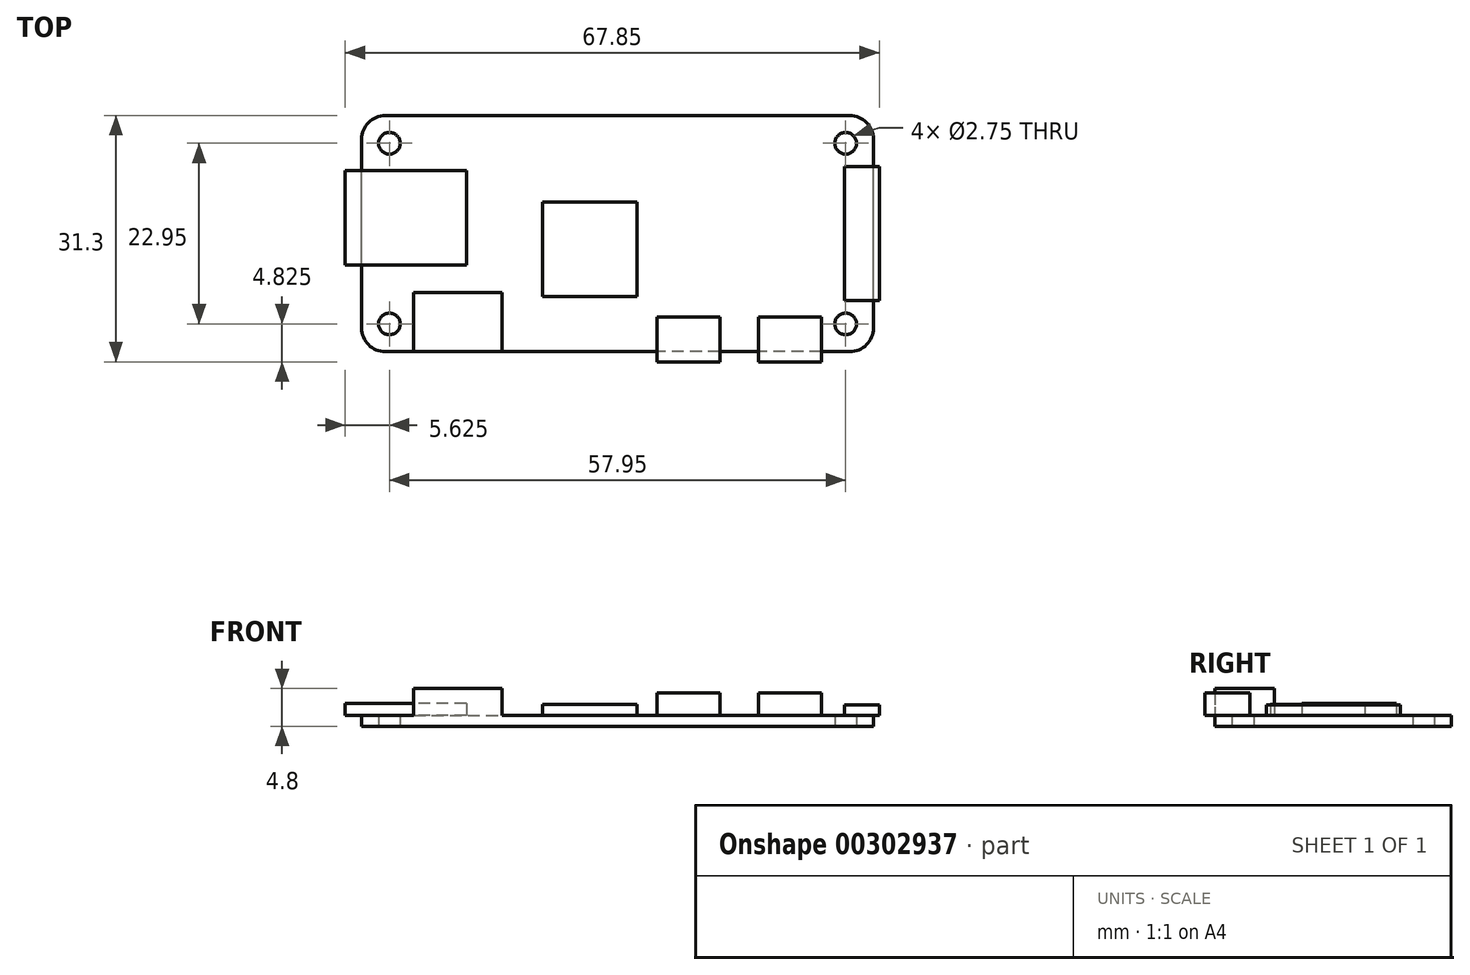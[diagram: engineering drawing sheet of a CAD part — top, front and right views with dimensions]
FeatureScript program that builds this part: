
annotation { "Feature Type Name" : "Feature", "Feature Type Description" : "" }
export const myFeature = defineFeature(function(context is Context, id is Id, definition is map)
    precondition{}
    {
        {
            var Q0;
            Q0=qCreatedBy(makeId("Top.planeOp"),FACE);
            var sketch = newSketch(context, id + "F0", { "sketchPlane" : qUnion([Q0])});
            skLineSegment(sketch, "E0.bottom", {"start": v(29.5, -15) * mm, "end": v(-29.5, -15) * mm});
            skLineSegment(sketch, "E0.top", {"start": v(29.5, 15) * mm, "end": v(-29.5, 15) * mm});
            skLineSegment(sketch, "E0.left", {"start": v(32.5, -12) * mm, "end": v(32.5, 12) * mm});
            skLineSegment(sketch, "E0.right", {"start": v(-32.5, -12) * mm, "end": v(-32.5, 12) * mm});
            skPoint(sketch, "E0.middle", {"position": v(0, 0) * mm});
            skCircle(sketch, "E1", {"center": v(-28.98, 11.47) * mm, "radius": 1.38 * mm});
            skCircle(sketch, "E2", {"center": v(28.98, 11.47) * mm, "radius": 1.38 * mm});
            skCircle(sketch, "E3", {"center": v(-28.98, -11.47) * mm, "radius": 1.38 * mm});
            skCircle(sketch, "E4", {"center": v(28.98, -11.47) * mm, "radius": 1.38 * mm});
            skPoint(sketch, "E5.visualSharp", {"position": v(-32.5, 15) * mm});
            skArc(sketch, "E5.filletArc", {"start": v(-29.5, 15) * mm, "mid": v(-31.62, 14.12) * mm, "end": v(-32.5, 12) * mm});
            skPoint(sketch, "E6.visualSharp", {"position": v(32.5, 15) * mm});
            skArc(sketch, "E6.filletArc", {"start": v(32.5, 12) * mm, "mid": v(31.62, 14.12) * mm, "end": v(29.5, 15) * mm});
            skPoint(sketch, "E7.visualSharp", {"position": v(32.5, -15) * mm});
            skArc(sketch, "E7.filletArc", {"start": v(29.5, -15) * mm, "mid": v(31.62, -14.12) * mm, "end": v(32.5, -12) * mm});
            skPoint(sketch, "E8.visualSharp", {"position": v(-32.5, -15) * mm});
            skArc(sketch, "E8.filletArc", {"start": v(-32.5, -12) * mm, "mid": v(-31.62, -14.12) * mm, "end": v(-29.5, -15) * mm});
            skSolve(sketch);
        }
        {
            var Q0;
            Q0=qSketchRegion(id+"F0",true);
            extrude(context, id + "F1", {"entities" : qUnion([Q0]), "depth" : 1.4 * mm});
        }
        {
            var Q0;
            Q0=makeQuery(id+"F1.opExtrude","CAP_FACE",FACE,{"disambiguationData":[OSD([sQuery(id+"F0.wireOp",EDGE,"E0.bottom"),sQuery(id+"F0.wireOp",EDGE,"E0.top"),sQuery(id+"F0.wireOp",EDGE,"E0.left"),sQuery(id+"F0.wireOp",EDGE,"E0.right"),sQuery(id+"F0.wireOp",EDGE,"E1"),sQuery(id+"F0.wireOp",EDGE,"E2"),sQuery(id+"F0.wireOp",EDGE,"E3"),sQuery(id+"F0.wireOp",EDGE,"E4"),sQuery(id+"F0.wireOp",EDGE,"E5.filletArc"),sQuery(id+"F0.wireOp",EDGE,"E6.filletArc"),sQuery(id+"F0.wireOp",EDGE,"E7.filletArc"),sQuery(id+"F0.wireOp",EDGE,"E8.filletArc")])],"isStart":false});
            var sketch = newSketch(context, id + "F2", { "sketchPlane" : qUnion([Q0])});
            skLineSegment(sketch, "E9.bottom", {"start": v(2.5, -8) * mm, "end": v(-9.5, -8) * mm});
            skLineSegment(sketch, "E9.top", {"start": v(2.5, 4) * mm, "end": v(-9.5, 4) * mm});
            skLineSegment(sketch, "E9.left", {"start": v(2.5, -8) * mm, "end": v(2.5, 4) * mm});
            skLineSegment(sketch, "E9.right", {"start": v(-9.5, -8) * mm, "end": v(-9.5, 4) * mm});
            skPoint(sketch, "E9.middle", {"position": v(-3.5, -2) * mm});
            skLineSegment(sketch, "E10.bottom", {"start": v(33.25, -8.5) * mm, "end": v(28.85, -8.5) * mm});
            skLineSegment(sketch, "E10.top", {"start": v(33.25, 8.5) * mm, "end": v(28.85, 8.5) * mm});
            skLineSegment(sketch, "E10.left", {"start": v(33.25, -8.5) * mm, "end": v(33.25, 8.5) * mm});
            skLineSegment(sketch, "E10.right", {"start": v(28.85, -8.5) * mm, "end": v(28.85, 8.5) * mm});
            skPoint(sketch, "E10.middle", {"position": v(31.05, 0) * mm});
            skPoint(sketch, "E11", {"position": v(32.5, 0) * mm});
            skLineSegment(sketch, "E12.bottom", {"start": v(-19.2, -4) * mm, "end": v(-34.6, -4) * mm});
            skLineSegment(sketch, "E12.top", {"start": v(-19.2, 8) * mm, "end": v(-34.6, 8) * mm});
            skLineSegment(sketch, "E12.left", {"start": v(-19.2, -4) * mm, "end": v(-19.2, 8) * mm});
            skLineSegment(sketch, "E12.right", {"start": v(-34.6, -4) * mm, "end": v(-34.6, 8) * mm});
            skPoint(sketch, "E12.middle", {"position": v(-26.9, 2) * mm});
            skLineSegment(sketch, "E13.bottom", {"start": v(-25.9, -15) * mm, "end": v(-14.7, -15) * mm});
            skLineSegment(sketch, "E13.top", {"start": v(-25.9, -7.5) * mm, "end": v(-14.7, -7.5) * mm});
            skLineSegment(sketch, "E13.left", {"start": v(-25.9, -15) * mm, "end": v(-25.9, -7.5) * mm});
            skLineSegment(sketch, "E13.right", {"start": v(-14.7, -15) * mm, "end": v(-14.7, -7.5) * mm});
            skLineSegment(sketch, "E14.bottom", {"start": v(5, -16.3) * mm, "end": v(13, -16.3) * mm});
            skLineSegment(sketch, "E14.top", {"start": v(5, -10.6) * mm, "end": v(13, -10.6) * mm});
            skLineSegment(sketch, "E14.left", {"start": v(5, -16.3) * mm, "end": v(5, -10.6) * mm});
            skLineSegment(sketch, "E14.right", {"start": v(13, -16.3) * mm, "end": v(13, -10.6) * mm});
            skLineSegment(sketch, "E15.bottom", {"start": v(17.9, -16.3) * mm, "end": v(25.9, -16.3) * mm});
            skLineSegment(sketch, "E15.top", {"start": v(17.9, -10.6) * mm, "end": v(25.9, -10.6) * mm});
            skLineSegment(sketch, "E15.left", {"start": v(17.9, -16.3) * mm, "end": v(17.9, -10.6) * mm});
            skLineSegment(sketch, "E15.right", {"start": v(25.9, -16.3) * mm, "end": v(25.9, -10.6) * mm});
            skSolve(sketch);
        }
        {
            var Q0;
            Q0=makeQuery(id+"F2.imprint","IMPRINT",FACE,{"disambiguationData":[TD([[makeQuery(id+"F2.imprint","IMPRINT",EDGE,{"derivedFrom":sQuery(id+"F2.wireOp",EDGE,"E9.bottom")}),-1.0]])]});
            extrude(context, id + "F3", {"entities" : qUnion([Q0]), "operationType" : NewBodyOperationType.ADD, "depth" : 1.4 * mm});
        }
        {
            var Q0;
            Q0=makeQuery(id+"F2.imprint","IMPRINT",FACE,{"disambiguationData":[TD([[makeQuery(id+"F2.imprint","IMPRINT",EDGE,{"derivedFrom":sQuery(id+"F2.wireOp",EDGE,"E13.bottom")}),-1.0]])]});
            extrude(context, id + "F4", {"entities" : qUnion([Q0]), "operationType" : NewBodyOperationType.ADD, "depth" : (4.8 - 1.4) * mm});
        }
        {
            var Q0;
            {var subQ0=sQuery(id+"F2.wireOp",EDGE,"E14.top");Q0=makeQuery(id+"F2.imprint","IMPRINT",FACE,{"disambiguationData":[TD([[makeQuery(id+"F2.imprint","IMPRINT",EDGE,{"derivedFrom":subQ0}),-1.0]])]});}
            var Q1;
            {var subQ0=sQuery(id+"F2.wireOp",EDGE,"E15.top");Q1=makeQuery(id+"F2.imprint","IMPRINT",FACE,{"disambiguationData":[TD([[makeQuery(id+"F2.imprint","IMPRINT",EDGE,{"derivedFrom":subQ0}),-1.0]])]});}
            var Q2;
            {var subQ0=sQuery(id+"F2.wireOp",EDGE,"E15.bottom");Q2=makeQuery(id+"F2.imprint","IMPRINT",FACE,{"disambiguationData":[TD([[makeQuery(id+"F2.imprint","IMPRINT",EDGE,{"derivedFrom":subQ0}),1.0]])]});}
            var Q3;
            {var subQ0=sQuery(id+"F2.wireOp",EDGE,"E14.bottom");Q3=makeQuery(id+"F2.imprint","IMPRINT",FACE,{"disambiguationData":[TD([[makeQuery(id+"F2.imprint","IMPRINT",EDGE,{"derivedFrom":subQ0}),1.0]])]});}
            extrude(context, id + "F5", {"entities" : qUnion([Q0, Q1, Q2, Q3]), "operationType" : NewBodyOperationType.ADD, "depth" : (4.25 - 1.4) * mm});
        }
        {
            var Q0;
            {var subQ0=sQuery(id+"F2.wireOp",EDGE,"E10.right");Q0=makeQuery(id+"F2.imprint","IMPRINT",FACE,{"disambiguationData":[TD([[makeQuery(id+"F2.imprint","IMPRINT",EDGE,{"derivedFrom":subQ0}),-1.0]])]});}
            var Q1;
            {var subQ0=sQuery(id+"F2.wireOp",EDGE,"E10.left");Q1=makeQuery(id+"F2.imprint","IMPRINT",FACE,{"disambiguationData":[TD([[makeQuery(id+"F2.imprint","IMPRINT",EDGE,{"derivedFrom":subQ0}),1.0]])]});}
            extrude(context, id + "F6", {"entities" : qUnion([Q0, Q1]), "operationType" : NewBodyOperationType.ADD, "depth" : (2.75 - 1.4) * mm});
        }
        {
            var Q0;
            {var subQ0=sQuery(id+"F2.wireOp",EDGE,"E12.right");Q0=makeQuery(id+"F2.imprint","IMPRINT",FACE,{"disambiguationData":[TD([[makeQuery(id+"F2.imprint","IMPRINT",EDGE,{"derivedFrom":subQ0}),-1.0]])]});}
            var Q1;
            {var subQ0=sQuery(id+"F2.wireOp",EDGE,"E12.left");Q1=makeQuery(id+"F2.imprint","IMPRINT",FACE,{"disambiguationData":[TD([[makeQuery(id+"F2.imprint","IMPRINT",EDGE,{"derivedFrom":subQ0}),1.0]])]});}
            extrude(context, id + "F7", {"entities" : qUnion([Q0, Q1]), "operationType" : NewBodyOperationType.ADD, "depth" : (2.9 - 1.4) * mm});
        }
    });
